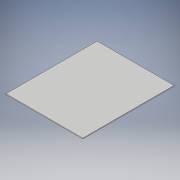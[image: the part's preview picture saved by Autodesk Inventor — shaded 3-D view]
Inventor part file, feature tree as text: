
AUTODESK INVENTOR PART (.ipt)
format: ipt  version: 2018 (Build 220112000, 112)  size: 90,624 bytes
history: native  units: mm
features: extrude x1, sketch x1
ambient origin geometry x8: Origin, YZ Plane, XZ Plane, XY Plane, X Axis, Y Axis, Z Axis, Center Point
bodies: Volumenkörper1 (feature_tree)
feature tree (2):
  extrude  "Extrusion1"  Depth=181.5mm
  sketch  "Skizze1"  dims[d0=153.0mm d1=181.5mm d2=1.5mm d3=0.0mm]
